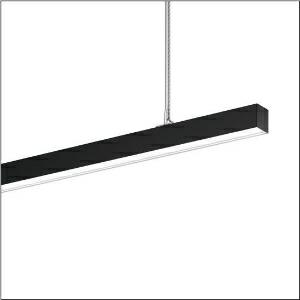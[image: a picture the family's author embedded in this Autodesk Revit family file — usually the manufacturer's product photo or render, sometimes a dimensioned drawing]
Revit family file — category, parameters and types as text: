
# Revit family: silica_r__21_51mx33da47bb_630a
name_source: partatom
category: Lighting Fixtures
units: mm (PartAtom-declared; Revit-internal decimal feet)

## family parameters
Cut with Voids When Loaded = No
Host = Face
Light Source = No
Part Type = Normal
Room Calculation Point = No
Round Connector Dimension = Use Diameter
Shared = No

## types (1)
- --- (1 x LED, 5910 lm, 38.4 W, 4000K)
    Apparent Load = 38 VA
    CIE Flux Codes = 78 96 99 55 100
    Color Rendering = 80
    Color Temperature = 4000K
    Default Elevation = 1800 mm
    Description = Silica® 21, office luminaire, primary optical cover: prismatic diffuser, of PMMA, CAT 2 (L<= 3000cd/m²), light emission: direct/indirect distribution, primary light characteristic: symmetric, installation type: suspended mounting, LED, rated luminous flux: 5.910lm, luminous efficacy: 154lm/W, light colour: 840, colour temperature: 4000K, control gear: DALI 2, with terminal, 3+2-pole, max. 2.5mm², mains connection: 220..240V, AC, 50/60Hz, rated input power: 38.4W, luminaire housing, of aluminium, matt jet black (RAL 9005), length: 1.204mm, width: 53mm, height: 53mm, protection rating (complete): IP20, insulation class (complete): insulation class I (protective earthing), certification: CE, permissible operating ambient temperature: 0..+35°C, standard: EN 50419, packaging unit: 1 piece
    Height = 53 mm
    Lamp = 1 x LED
    Lamp Light Flux = 5910 lm
    Lamp Power = 38.4 W
    Lamp count = 1
    Length = 1204 mm
    Luminous efficacy = 154 lm/W
    Manufacturer = Siteco
    ModVariant = No
    Model = 51MX33DA47BB
    Mounting Place = Ceiling
    Mounting Type = Pendant
    Number of Poles = 1
    OnlyDefault = Yes
    Power Factor = 1
    Product Name = Silica® 21
    Product group = office luminaire | ceiling pendant
    ProductGroupID = 904
    Protection Class = Protection class I
    Protection Degree = IP 20
    RLX_Detail_Level = 1
    RLX_Emergency_Light_Flux = 0 lm
    RLX_Emergency_Type = 0
    RLX_Emergency_Type_DB = No
    RlxData = <blob elided: 25937 chars, md5=858b494d>
    Socket = socket
    Standby Power = 0 W
    System Light Flux = 5910 lm
    System Power = 38 W
    Type Comments = factory setting: luminous flux: 100 % | dim-lin: 254 | 322 mA
    Type Image = l_1335856.jpg
    URL = http://relux.com
    VarID = @adj_118754
    Voltage = 0 V
    Weight = 0.00 kg
    Width = 53 mm

## geometry (parser evidence)
native form markers: Blend x4, Sweep x13
no freeform markers — native parametric forms only
